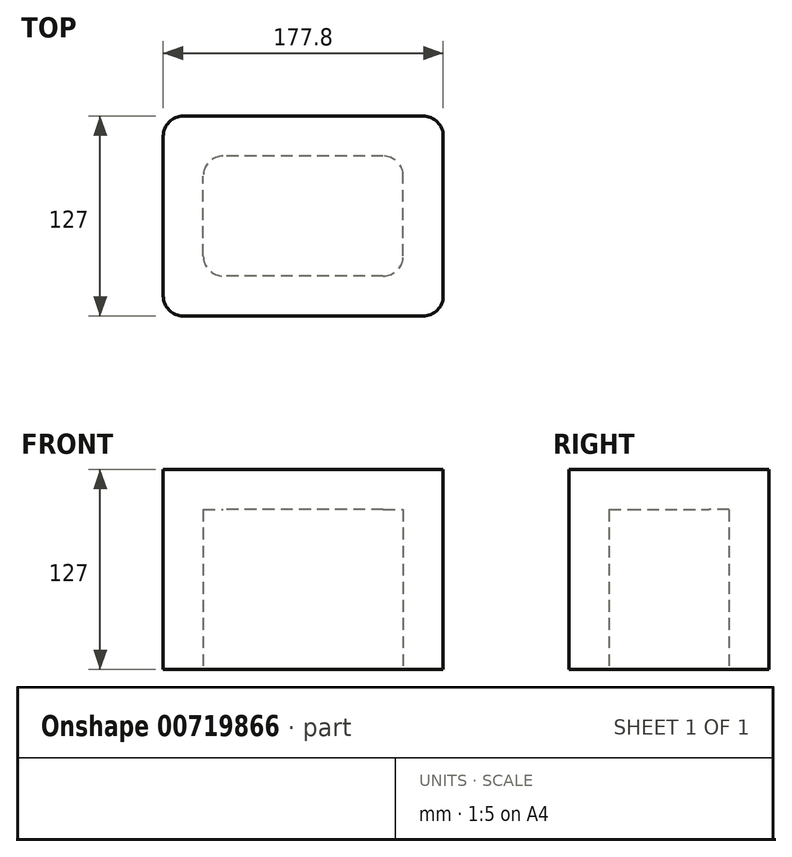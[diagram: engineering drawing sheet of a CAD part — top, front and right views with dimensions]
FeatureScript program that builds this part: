
annotation { "Feature Type Name" : "Feature", "Feature Type Description" : "" }
export const myFeature = defineFeature(function(context is Context, id is Id, definition is map)
    precondition{}
    {
        {
            var Q0;
            Q0=qCreatedBy(makeId("Top.planeOp"),FACE);
            var sketch = newSketch(context, id + "F0", { "sketchPlane" : qUnion([Q0])});
            skLineSegment(sketch, "E0.bottom", {"start": v(96.46, 43.4) * mm, "end": v(-81.34, 43.4) * mm});
            skLineSegment(sketch, "E0.top", {"start": v(96.46, -83.6) * mm, "end": v(-81.34, -83.6) * mm});
            skLineSegment(sketch, "E0.left", {"start": v(96.46, 43.4) * mm, "end": v(96.46, -83.6) * mm});
            skLineSegment(sketch, "E0.right", {"start": v(-81.34, 43.4) * mm, "end": v(-81.34, -83.6) * mm});
            skLineSegment(sketch, "E1.bottom", {"start": v(71.06, -58.2) * mm, "end": v(-55.94, -58.2) * mm});
            skLineSegment(sketch, "E1.top", {"start": v(71.06, 18) * mm, "end": v(-55.94, 18) * mm});
            skLineSegment(sketch, "E1.left", {"start": v(71.06, -58.2) * mm, "end": v(71.06, 18) * mm});
            skLineSegment(sketch, "E1.right", {"start": v(-55.94, -58.2) * mm, "end": v(-55.94, 18) * mm});
            skSolve(sketch);
        }
        {
            var Q0;
            Q0=makeQuery(id+"F0.imprint","IMPRINT",FACE,{"disambiguationData":[TD([[makeQuery(id+"F0.imprint","IMPRINT",EDGE,{"derivedFrom":sQuery(id+"F0.wireOp",EDGE,"E0.bottom")}),1.0]])]});
            var Q1;
            Q1=makeQuery(id+"F0.imprint","IMPRINT",FACE,{"disambiguationData":[TD([[makeQuery(id+"F0.imprint","IMPRINT",EDGE,{"derivedFrom":sQuery(id+"F0.wireOp",EDGE,"E1.bottom")}),-1.0]])]});
            extrude(context, id + "F1", {"entities" : qUnion([Q0, Q1]), "depth" : 127 * mm, "offsetDistance" : 25.4 * mm});
        }
        {
            var Q0;
            Q0=makeQuery(id+"F0.imprint","IMPRINT",FACE,{"disambiguationData":[TD([[makeQuery(id+"F0.imprint","IMPRINT",EDGE,{"derivedFrom":sQuery(id+"F0.wireOp",EDGE,"E1.bottom")}),-1.0]])]});
            extrude(context, id + "F2", {"entities" : qUnion([Q0]), "operationType" : NewBodyOperationType.REMOVE, "depth" : 101.6 * mm, "offsetDistance" : 25.4 * mm});
        }
        {
            var Q0;
            Q0=makeQuery(id+"F2.boolean.opBoolean","COPY",EDGE,{"derivedFrom":makeQuery(id+"F2.opExtrude","SWEPT_EDGE",EDGE,{"disambiguationData":[OSD([sQuery(id+"F0.wireOp",EDGE,"E1.top"),sQuery(id+"F0.wireOp",EDGE,"E1.right")])]})});
            var Q1;
            Q1=makeQuery(id+"F2.boolean.opBoolean","COPY",EDGE,{"derivedFrom":makeQuery(id+"F2.opExtrude","SWEPT_EDGE",EDGE,{"disambiguationData":[OSD([sQuery(id+"F0.wireOp",EDGE,"E1.bottom"),sQuery(id+"F0.wireOp",EDGE,"E1.right")])]})});
            var Q2;
            Q2=makeQuery(id+"F2.boolean.opBoolean","COPY",EDGE,{"derivedFrom":makeQuery(id+"F2.opExtrude","SWEPT_EDGE",EDGE,{"disambiguationData":[OSD([sQuery(id+"F0.wireOp",EDGE,"E1.top"),sQuery(id+"F0.wireOp",EDGE,"E1.left")])]})});
            var Q3;
            Q3=makeQuery(id+"F2.boolean.opBoolean","COPY",EDGE,{"derivedFrom":makeQuery(id+"F2.opExtrude","SWEPT_EDGE",EDGE,{"disambiguationData":[OSD([sQuery(id+"F0.wireOp",EDGE,"E1.bottom"),sQuery(id+"F0.wireOp",EDGE,"E1.left")])]})});
            fillet(context, id + "F3", {"entities" : qUnion([Q0, Q1, Q2, Q3]), "radius" : 12.7 * mm, "tangentPropagation" : true, "allowEdgeOverflow" : false});
        }
        {
            var Q0;
            Q0=makeQuery(id+"F1.opExtrude","SWEPT_EDGE",EDGE,{"disambiguationData":[OSD([sQuery(id+"F0.wireOp",EDGE,"E0.top"),sQuery(id+"F0.wireOp",EDGE,"E0.left")])]});
            var Q1;
            Q1=makeQuery(id+"F1.opExtrude","SWEPT_EDGE",EDGE,{"disambiguationData":[OSD([sQuery(id+"F0.wireOp",EDGE,"E0.bottom"),sQuery(id+"F0.wireOp",EDGE,"E0.left")])]});
            var Q2;
            Q2=makeQuery(id+"F1.opExtrude","SWEPT_EDGE",EDGE,{"disambiguationData":[OSD([sQuery(id+"F0.wireOp",EDGE,"E0.top"),sQuery(id+"F0.wireOp",EDGE,"E0.right")])]});
            var Q3;
            Q3=makeQuery(id+"F1.opExtrude","SWEPT_EDGE",EDGE,{"disambiguationData":[OSD([sQuery(id+"F0.wireOp",EDGE,"E0.bottom"),sQuery(id+"F0.wireOp",EDGE,"E0.right")])]});
            fillet(context, id + "F4", {"entities" : qUnion([Q0, Q1, Q2, Q3]), "radius" : 12.7 * mm, "tangentPropagation" : true, "allowEdgeOverflow" : false});
        }
    });
